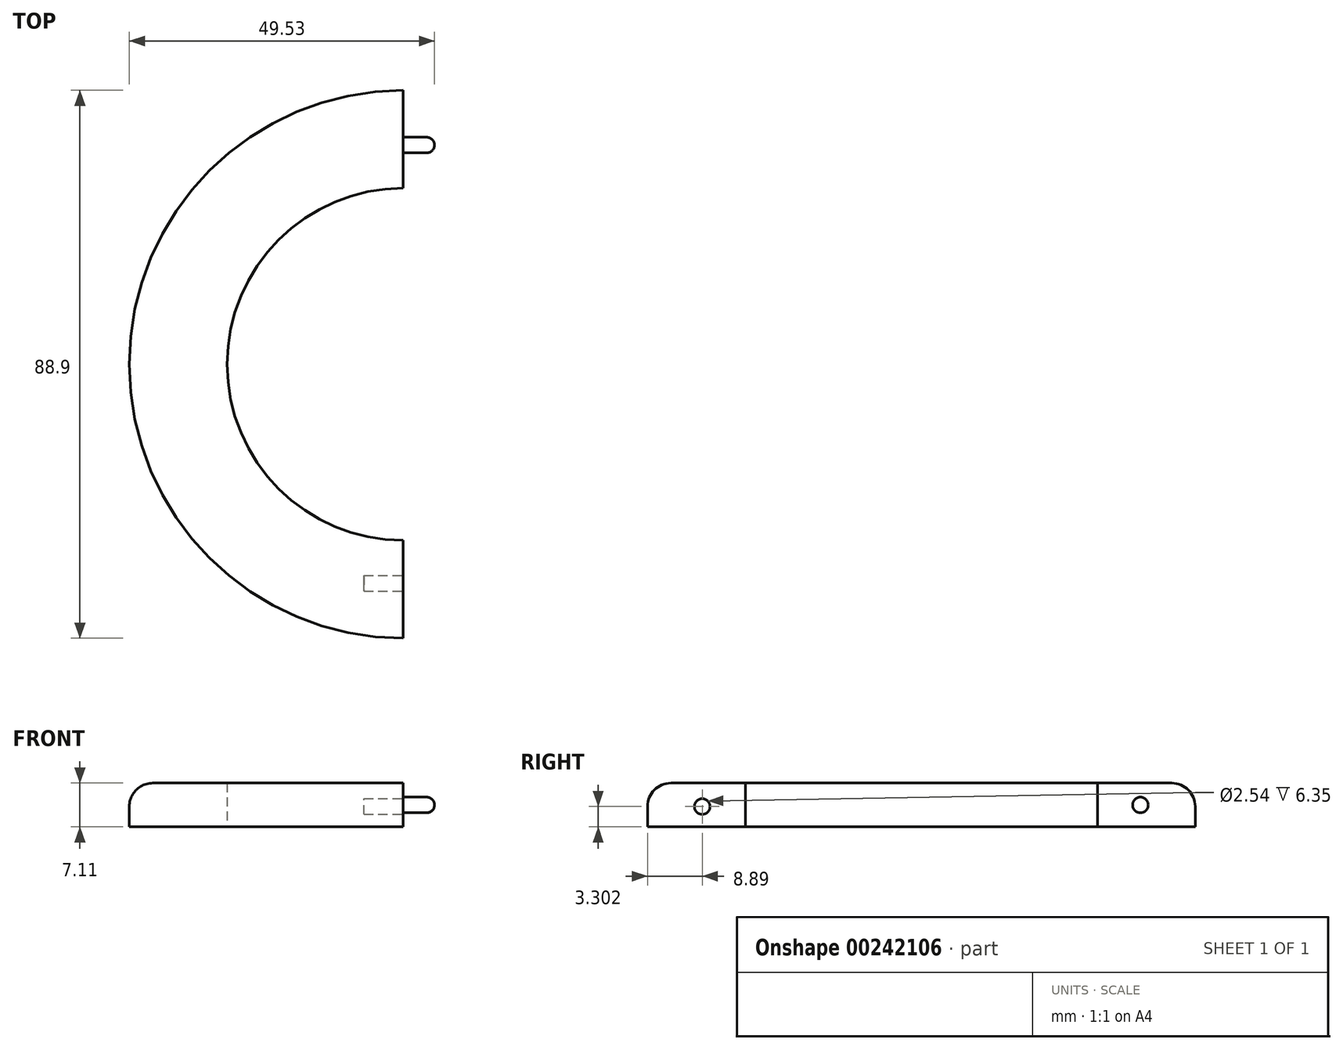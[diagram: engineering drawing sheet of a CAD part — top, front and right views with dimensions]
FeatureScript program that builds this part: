
annotation { "Feature Type Name" : "Feature", "Feature Type Description" : "" }
export const myFeature = defineFeature(function(context is Context, id is Id, definition is map)
    precondition{}
    {
        {
            var Q0;
            Q0=qCreatedBy(makeId("Top.planeOp"),FACE);
            var sketch = newSketch(context, id + "F0", { "sketchPlane" : qUnion([Q0])});
            skCircle(sketch, "E0", {"center": v(0, 0) * mm, "radius": 44.45 * mm});
            skCircle(sketch, "E1", {"center": v(0, 0) * mm, "radius": 28.58 * mm});
            skSolve(sketch);
        }
        {
            var Q0;
            Q0=makeQuery(id+"F0.imprint","IMPRINT",FACE,{"disambiguationData":[TD([[makeQuery(id+"F0.imprint","IMPRINT",EDGE,{"derivedFrom":sQuery(id+"F0.wireOp",EDGE,"E0")}),1.0]])]});
            extrude(context, id + "F1", {"entities" : qUnion([Q0]), "depth" : 7.11 * mm});
        }
        {
            var Q0;
            Q0=makeQuery(id+"F1.opExtrude","CAP_EDGE",EDGE,{"disambiguationData":[OSD([sQuery(id+"F0.wireOp",EDGE,"E0")])],"isStart":false});
            fillet(context, id + "F2", {"entities" : qUnion([Q0]), "radius" : 3.8 * mm, "tangentPropagation" : true, "allowEdgeOverflow" : false});
        }
        {
            var Q0;
            Q0=qCreatedBy(makeId("Top.planeOp"),FACE);
            var sketch = newSketch(context, id + "F3", { "sketchPlane" : qUnion([Q0])});
            skLineSegment(sketch, "E2.bottom", {"start": v(0, 63.8) * mm, "end": v(80.15, 63.8) * mm});
            skLineSegment(sketch, "E2.top", {"start": v(0, -66.7) * mm, "end": v(80.15, -66.7) * mm});
            skLineSegment(sketch, "E2.left", {"start": v(0, 63.8) * mm, "end": v(0, -66.7) * mm});
            skLineSegment(sketch, "E2.right", {"start": v(80.15, 63.8) * mm, "end": v(80.15, -66.7) * mm});
            skSolve(sketch);
        }
        {
            var Q0;
            Q0 = qSketchRegion(id + "F3", true);
            extrude(context, id + "F4", {"entities" : qUnion([Q0]), "operationType" : NewBodyOperationType.REMOVE, "endBound" : BoundingType.SYMMETRIC, "oppositeDirection" : true, "depth" : 25.4 * mm});
        }
        {
            var Q0;
            Q0=makeQuery(id+"F4.boolean.opBoolean","COPY",FACE,{"disambiguationData":[OD(0.0)],"derivedFrom":makeQuery(id+"F4.opExtrude","SWEPT_FACE",FACE,{"disambiguationData":[OSD([sQuery(id+"F3.wireOp",EDGE,"E2.left")])]})});
            var sketch = newSketch(context, id + "F5", { "sketchPlane" : qUnion([Q0])});
            skCircle(sketch, "E3", {"center": v(-35.56, 3.3) * mm, "radius": 1.27 * mm});
            skSolve(sketch);
        }
        {
            var Q0;
            Q0=makeQuery(id+"F4.boolean.opBoolean","COPY",FACE,{"disambiguationData":[OD(1.0)],"derivedFrom":makeQuery(id+"F4.opExtrude","SWEPT_FACE",FACE,{"disambiguationData":[OSD([sQuery(id+"F3.wireOp",EDGE,"E2.left")])]})});
            var sketch = newSketch(context, id + "F6", { "sketchPlane" : qUnion([Q0])});
            skCircle(sketch, "E4", {"center": v(35.56, 3.56) * mm, "radius": 1.27 * mm});
            skSolve(sketch);
        }
        {
            var Q0;
            Q0 = qSketchRegion(id + "F6", true);
            extrude(context, id + "F7", {"entities" : qUnion([Q0]), "operationType" : NewBodyOperationType.ADD, "depth" : 5.08 * mm});
        }
        {
            var Q0;
            Q0=makeQuery(id+"F5.imprint","IMPRINT",FACE,{"disambiguationData":[TD([[makeQuery(id+"F5.imprint","IMPRINT",EDGE,{"derivedFrom":sQuery(id+"F5.wireOp",EDGE,"E3")}),1.0]])]});
            extrude(context, id + "F8", {"entities" : qUnion([Q0]), "operationType" : NewBodyOperationType.REMOVE, "oppositeDirection" : true, "depth" : 6.35 * mm});
        }
        {
            var Q0;
            Q0=makeQuery(id+"F7.opExtrude","CAP_FACE",FACE,{"disambiguationData":[OSD([sQuery(id+"F6.wireOp",EDGE,"E4")])],"isStart":false});
            var Q1;
            Q1=makeQuery(id+"F8.boolean.opBoolean","COPY",EDGE,{"derivedFrom":makeQuery(id+"F8.opExtrude","CAP_EDGE",EDGE,{"disambiguationData":[OSD([sQuery(id+"F5.wireOp",EDGE,"E3")])],"isStart":true})});
            fillet(context, id + "F9", {"entities" : qUnion([Q0, Q1]), "radius" : 1.27 * mm, "tangentPropagation" : true, "allowEdgeOverflow" : false});
        }
    });
